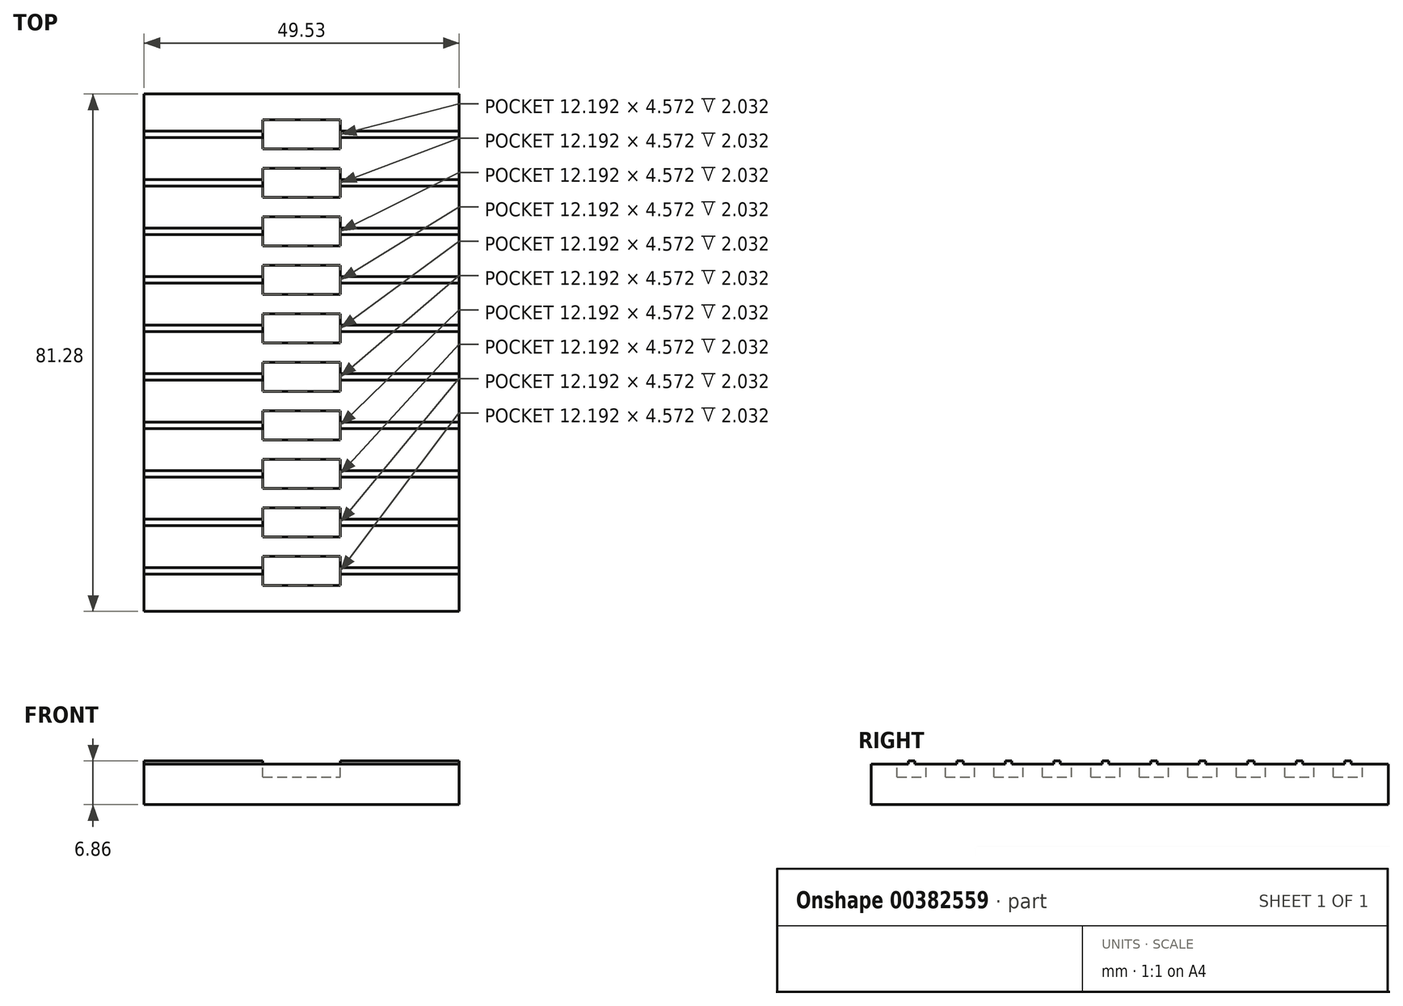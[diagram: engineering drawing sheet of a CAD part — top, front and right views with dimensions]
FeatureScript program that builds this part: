
annotation { "Feature Type Name" : "Feature", "Feature Type Description" : "" }
export const myFeature = defineFeature(function(context is Context, id is Id, definition is map)
    precondition{}
    {
        {
            var Q0;
            Q0=qCreatedBy(makeId("Top.planeOp"),FACE);
            var sketch = newSketch(context, id + "F0", { "sketchPlane" : qUnion([Q0])});
            skLineSegment(sketch, "E0.bottom", {"start": v(0, 0) * mm, "end": v(49.53, 0) * mm});
            skLineSegment(sketch, "E0.top", {"start": v(0, 81.28) * mm, "end": v(49.53, 81.28) * mm});
            skLineSegment(sketch, "E0.left", {"start": v(0, 0) * mm, "end": v(0, 81.28) * mm});
            skLineSegment(sketch, "E0.right", {"start": v(49.53, 0) * mm, "end": v(49.53, 81.28) * mm});
            skSolve(sketch);
        }
        {
            var Q0;
            Q0=qSketchRegion(id+"F0",true);
            extrude(context, id + "F1", {"entities" : qUnion([Q0]), "depth" : 6.35 * mm});
        }
        {
            var Q0;
            Q0=makeQuery(id+"F1.opExtrude","CAP_FACE",FACE,{"disambiguationData":[OSD([sQuery(id+"F0.wireOp",EDGE,"E0.bottom"),sQuery(id+"F0.wireOp",EDGE,"E0.top"),sQuery(id+"F0.wireOp",EDGE,"E0.left"),sQuery(id+"F0.wireOp",EDGE,"E0.right")])],"isStart":false});
            var sketch = newSketch(context, id + "F2", { "sketchPlane" : qUnion([Q0])});
            skLineSegment(sketch, "E1.bottom", {"start": v(18.67, 4.06) * mm, "end": v(30.86, 4.06) * mm});
            skLineSegment(sketch, "E1.top", {"start": v(18.67, 8.64) * mm, "end": v(30.86, 8.64) * mm});
            skLineSegment(sketch, "E1.left", {"start": v(18.67, 4.06) * mm, "end": v(18.67, 8.64) * mm});
            skLineSegment(sketch, "E1.right", {"start": v(30.86, 4.06) * mm, "end": v(30.86, 8.64) * mm});
            skLineSegment(sketch, "E2", {"start": v(30.86, 6.35) * mm, "end": v(49.53, 6.35) * mm, "construction": true});
            skLineSegment(sketch, "E3.0.1.0", {"start": v(18.67, 16.26) * mm, "end": v(30.86, 16.26) * mm});
            skLineSegment(sketch, "E3.0.1.1", {"start": v(18.67, 11.68) * mm, "end": v(30.86, 11.68) * mm});
            skLineSegment(sketch, "E3.0.1.2", {"start": v(30.86, 11.68) * mm, "end": v(30.86, 16.26) * mm});
            skLineSegment(sketch, "E3.0.1.3", {"start": v(18.67, 11.68) * mm, "end": v(18.67, 16.26) * mm});
            skLineSegment(sketch, "E3.0.2.0", {"start": v(18.67, 23.88) * mm, "end": v(30.86, 23.88) * mm});
            skLineSegment(sketch, "E3.0.2.1", {"start": v(18.67, 19.3) * mm, "end": v(30.86, 19.3) * mm});
            skLineSegment(sketch, "E3.0.2.2", {"start": v(30.86, 19.3) * mm, "end": v(30.86, 23.88) * mm});
            skLineSegment(sketch, "E3.0.2.3", {"start": v(18.67, 19.3) * mm, "end": v(18.67, 23.88) * mm});
            skLineSegment(sketch, "E3.0.3.0", {"start": v(18.67, 31.5) * mm, "end": v(30.86, 31.5) * mm});
            skLineSegment(sketch, "E3.0.3.1", {"start": v(18.67, 26.92) * mm, "end": v(30.86, 26.92) * mm});
            skLineSegment(sketch, "E3.0.3.2", {"start": v(30.86, 26.92) * mm, "end": v(30.86, 31.5) * mm});
            skLineSegment(sketch, "E3.0.3.3", {"start": v(18.67, 26.92) * mm, "end": v(18.67, 31.5) * mm});
            skLineSegment(sketch, "E3.0.4.0", {"start": v(18.67, 39.12) * mm, "end": v(30.86, 39.12) * mm});
            skLineSegment(sketch, "E3.0.4.1", {"start": v(18.67, 34.54) * mm, "end": v(30.86, 34.54) * mm});
            skLineSegment(sketch, "E3.0.4.2", {"start": v(30.86, 34.54) * mm, "end": v(30.86, 39.12) * mm});
            skLineSegment(sketch, "E3.0.4.3", {"start": v(18.67, 34.54) * mm, "end": v(18.67, 39.12) * mm});
            skLineSegment(sketch, "E3.0.5.0", {"start": v(18.67, 46.74) * mm, "end": v(30.86, 46.74) * mm});
            skLineSegment(sketch, "E3.0.5.1", {"start": v(18.67, 42.16) * mm, "end": v(30.86, 42.16) * mm});
            skLineSegment(sketch, "E3.0.5.2", {"start": v(30.86, 42.16) * mm, "end": v(30.86, 46.74) * mm});
            skLineSegment(sketch, "E3.0.5.3", {"start": v(18.67, 42.16) * mm, "end": v(18.67, 46.74) * mm});
            skLineSegment(sketch, "E3.0.6.0", {"start": v(18.67, 54.36) * mm, "end": v(30.86, 54.36) * mm});
            skLineSegment(sketch, "E3.0.6.1", {"start": v(18.67, 49.78) * mm, "end": v(30.86, 49.78) * mm});
            skLineSegment(sketch, "E3.0.6.2", {"start": v(30.86, 49.78) * mm, "end": v(30.86, 54.36) * mm});
            skLineSegment(sketch, "E3.0.6.3", {"start": v(18.67, 49.78) * mm, "end": v(18.67, 54.36) * mm});
            skLineSegment(sketch, "E3.0.7.0", {"start": v(18.67, 61.98) * mm, "end": v(30.86, 61.98) * mm});
            skLineSegment(sketch, "E3.0.7.1", {"start": v(18.67, 57.4) * mm, "end": v(30.86, 57.4) * mm});
            skLineSegment(sketch, "E3.0.7.2", {"start": v(30.86, 57.4) * mm, "end": v(30.86, 61.98) * mm});
            skLineSegment(sketch, "E3.0.7.3", {"start": v(18.67, 57.4) * mm, "end": v(18.67, 61.98) * mm});
            skLineSegment(sketch, "E3.0.8.0", {"start": v(18.67, 69.6) * mm, "end": v(30.86, 69.6) * mm});
            skLineSegment(sketch, "E3.0.8.1", {"start": v(18.67, 65.02) * mm, "end": v(30.86, 65.02) * mm});
            skLineSegment(sketch, "E3.0.8.2", {"start": v(30.86, 65.02) * mm, "end": v(30.86, 69.6) * mm});
            skLineSegment(sketch, "E3.0.8.3", {"start": v(18.67, 65.02) * mm, "end": v(18.67, 69.6) * mm});
            skLineSegment(sketch, "E3.0.9.0", {"start": v(18.67, 77.22) * mm, "end": v(30.86, 77.22) * mm});
            skLineSegment(sketch, "E3.0.9.1", {"start": v(18.67, 72.64) * mm, "end": v(30.86, 72.64) * mm});
            skLineSegment(sketch, "E3.0.9.2", {"start": v(30.86, 72.64) * mm, "end": v(30.86, 77.22) * mm});
            skLineSegment(sketch, "E3.0.9.3", {"start": v(18.67, 72.64) * mm, "end": v(18.67, 77.22) * mm});
            skLineSegment(sketch, "E3.direction1", {"start": v(18.67, 4.06) * mm, "end": v(44.2, 4.06) * mm, "construction": true});
            skLineSegment(sketch, "E3.direction2", {"start": v(18.67, 4.06) * mm, "end": v(18.67, 11.68) * mm, "construction": true});
            skSolve(sketch);
        }
        {
            var Q0;
            Q0=qSketchRegion(id+"F2",true);
            extrude(context, id + "F3", {"entities" : qUnion([Q0]), "operationType" : NewBodyOperationType.REMOVE, "oppositeDirection" : true, "depth" : 2.03 * mm});
        }
        {
            var Q0;
            Q0=makeQuery(id+"F1.opExtrude","CAP_FACE",FACE,{"disambiguationData":[OSD([sQuery(id+"F0.wireOp",EDGE,"E0.bottom"),sQuery(id+"F0.wireOp",EDGE,"E0.top"),sQuery(id+"F0.wireOp",EDGE,"E0.left"),sQuery(id+"F0.wireOp",EDGE,"E0.right")])],"isStart":false});
            var sketch = newSketch(context, id + "F4", { "sketchPlane" : qUnion([Q0])});
            skLineSegment(sketch, "E4.bottom", {"start": v(30.86, 5.84) * mm, "end": v(49.53, 5.84) * mm});
            skLineSegment(sketch, "E4.top", {"start": v(30.86, 6.86) * mm, "end": v(49.53, 6.86) * mm});
            skLineSegment(sketch, "E4.left", {"start": v(30.86, 5.84) * mm, "end": v(30.86, 6.86) * mm});
            skLineSegment(sketch, "E4.right", {"start": v(49.53, 5.84) * mm, "end": v(49.53, 6.86) * mm});
            skPoint(sketch, "E5.firstSnap0", {"position": v(40.2, 6.86) * mm});
            skLineSegment(sketch, "E5.bottom", {"start": v(18.67, 6.86) * mm, "end": v(0, 6.86) * mm});
            skLineSegment(sketch, "E5.top", {"start": v(18.67, 5.84) * mm, "end": v(0, 5.84) * mm});
            skLineSegment(sketch, "E5.left", {"start": v(18.67, 6.86) * mm, "end": v(18.67, 5.84) * mm});
            skLineSegment(sketch, "E5.right", {"start": v(0, 6.86) * mm, "end": v(0, 5.84) * mm});
            skLineSegment(sketch, "E6", {"start": v(30.86, 6.35) * mm, "end": v(49.53, 6.35) * mm, "construction": true});
            skLineSegment(sketch, "E7.0.1.0", {"start": v(18.67, 13.46) * mm, "end": v(0, 13.46) * mm});
            skLineSegment(sketch, "E7.0.1.1", {"start": v(30.86, 13.97) * mm, "end": v(49.53, 13.97) * mm, "construction": true});
            skLineSegment(sketch, "E7.0.1.2", {"start": v(18.67, 14.48) * mm, "end": v(0, 14.48) * mm});
            skLineSegment(sketch, "E7.0.1.3", {"start": v(30.86, 14.48) * mm, "end": v(49.53, 14.48) * mm});
            skLineSegment(sketch, "E7.0.1.4", {"start": v(30.86, 13.46) * mm, "end": v(49.53, 13.46) * mm});
            skPoint(sketch, "E7.0.1.5", {"position": v(40.2, 14.48) * mm});
            skLineSegment(sketch, "E7.0.1.6", {"start": v(18.67, 14.48) * mm, "end": v(18.67, 13.46) * mm});
            skLineSegment(sketch, "E7.0.1.7", {"start": v(0, 14.48) * mm, "end": v(0, 13.46) * mm});
            skLineSegment(sketch, "E7.0.1.8", {"start": v(49.53, 13.46) * mm, "end": v(49.53, 14.48) * mm});
            skLineSegment(sketch, "E7.0.1.9", {"start": v(30.86, 13.46) * mm, "end": v(30.86, 14.48) * mm});
            skLineSegment(sketch, "E7.0.2.0", {"start": v(18.67, 21.08) * mm, "end": v(0, 21.08) * mm});
            skLineSegment(sketch, "E7.0.2.1", {"start": v(30.86, 21.6) * mm, "end": v(49.53, 21.6) * mm, "construction": true});
            skLineSegment(sketch, "E7.0.2.2", {"start": v(18.67, 22.1) * mm, "end": v(0, 22.1) * mm});
            skLineSegment(sketch, "E7.0.2.3", {"start": v(30.86, 22.1) * mm, "end": v(49.53, 22.1) * mm});
            skLineSegment(sketch, "E7.0.2.4", {"start": v(30.86, 21.08) * mm, "end": v(49.53, 21.08) * mm});
            skPoint(sketch, "E7.0.2.5", {"position": v(40.2, 22.1) * mm});
            skLineSegment(sketch, "E7.0.2.6", {"start": v(18.67, 22.1) * mm, "end": v(18.67, 21.08) * mm});
            skLineSegment(sketch, "E7.0.2.7", {"start": v(0, 22.1) * mm, "end": v(0, 21.08) * mm});
            skLineSegment(sketch, "E7.0.2.8", {"start": v(49.53, 21.08) * mm, "end": v(49.53, 22.1) * mm});
            skLineSegment(sketch, "E7.0.2.9", {"start": v(30.86, 21.08) * mm, "end": v(30.86, 22.1) * mm});
            skLineSegment(sketch, "E7.0.3.0", {"start": v(18.67, 28.7) * mm, "end": v(0, 28.7) * mm});
            skLineSegment(sketch, "E7.0.3.1", {"start": v(30.86, 29.21) * mm, "end": v(49.53, 29.21) * mm, "construction": true});
            skLineSegment(sketch, "E7.0.3.2", {"start": v(18.67, 29.72) * mm, "end": v(0, 29.72) * mm});
            skLineSegment(sketch, "E7.0.3.3", {"start": v(30.86, 29.72) * mm, "end": v(49.53, 29.72) * mm});
            skLineSegment(sketch, "E7.0.3.4", {"start": v(30.86, 28.7) * mm, "end": v(49.53, 28.7) * mm});
            skPoint(sketch, "E7.0.3.5", {"position": v(40.2, 29.72) * mm});
            skLineSegment(sketch, "E7.0.3.6", {"start": v(18.67, 29.72) * mm, "end": v(18.67, 28.7) * mm});
            skLineSegment(sketch, "E7.0.3.7", {"start": v(0, 29.72) * mm, "end": v(0, 28.7) * mm});
            skLineSegment(sketch, "E7.0.3.8", {"start": v(49.53, 28.7) * mm, "end": v(49.53, 29.72) * mm});
            skLineSegment(sketch, "E7.0.3.9", {"start": v(30.86, 28.7) * mm, "end": v(30.86, 29.72) * mm});
            skLineSegment(sketch, "E7.0.4.0", {"start": v(18.67, 36.32) * mm, "end": v(0, 36.32) * mm});
            skLineSegment(sketch, "E7.0.4.1", {"start": v(30.86, 36.83) * mm, "end": v(49.53, 36.83) * mm, "construction": true});
            skLineSegment(sketch, "E7.0.4.2", {"start": v(18.67, 37.34) * mm, "end": v(0, 37.34) * mm});
            skLineSegment(sketch, "E7.0.4.3", {"start": v(30.86, 37.34) * mm, "end": v(49.53, 37.34) * mm});
            skLineSegment(sketch, "E7.0.4.4", {"start": v(30.86, 36.32) * mm, "end": v(49.53, 36.32) * mm});
            skPoint(sketch, "E7.0.4.5", {"position": v(40.2, 37.34) * mm});
            skLineSegment(sketch, "E7.0.4.6", {"start": v(18.67, 37.34) * mm, "end": v(18.67, 36.32) * mm});
            skLineSegment(sketch, "E7.0.4.7", {"start": v(0, 37.34) * mm, "end": v(0, 36.32) * mm});
            skLineSegment(sketch, "E7.0.4.8", {"start": v(49.53, 36.32) * mm, "end": v(49.53, 37.34) * mm});
            skLineSegment(sketch, "E7.0.4.9", {"start": v(30.86, 36.32) * mm, "end": v(30.86, 37.34) * mm});
            skLineSegment(sketch, "E7.0.5.0", {"start": v(18.67, 43.94) * mm, "end": v(0, 43.94) * mm});
            skLineSegment(sketch, "E7.0.5.1", {"start": v(30.86, 44.45) * mm, "end": v(49.53, 44.45) * mm, "construction": true});
            skLineSegment(sketch, "E7.0.5.2", {"start": v(18.67, 44.96) * mm, "end": v(0, 44.96) * mm});
            skLineSegment(sketch, "E7.0.5.3", {"start": v(30.86, 44.96) * mm, "end": v(49.53, 44.96) * mm});
            skLineSegment(sketch, "E7.0.5.4", {"start": v(30.86, 43.94) * mm, "end": v(49.53, 43.94) * mm});
            skPoint(sketch, "E7.0.5.5", {"position": v(40.2, 44.96) * mm});
            skLineSegment(sketch, "E7.0.5.6", {"start": v(18.67, 44.96) * mm, "end": v(18.67, 43.94) * mm});
            skLineSegment(sketch, "E7.0.5.7", {"start": v(0, 44.96) * mm, "end": v(0, 43.94) * mm});
            skLineSegment(sketch, "E7.0.5.8", {"start": v(49.53, 43.94) * mm, "end": v(49.53, 44.96) * mm});
            skLineSegment(sketch, "E7.0.5.9", {"start": v(30.86, 43.94) * mm, "end": v(30.86, 44.96) * mm});
            skLineSegment(sketch, "E7.0.6.0", {"start": v(18.67, 51.56) * mm, "end": v(0, 51.56) * mm});
            skLineSegment(sketch, "E7.0.6.1", {"start": v(30.86, 52.07) * mm, "end": v(49.53, 52.07) * mm, "construction": true});
            skLineSegment(sketch, "E7.0.6.2", {"start": v(18.67, 52.58) * mm, "end": v(0, 52.58) * mm});
            skLineSegment(sketch, "E7.0.6.3", {"start": v(30.86, 52.58) * mm, "end": v(49.53, 52.58) * mm});
            skLineSegment(sketch, "E7.0.6.4", {"start": v(30.86, 51.56) * mm, "end": v(49.53, 51.56) * mm});
            skPoint(sketch, "E7.0.6.5", {"position": v(40.2, 52.58) * mm});
            skLineSegment(sketch, "E7.0.6.6", {"start": v(18.67, 52.58) * mm, "end": v(18.67, 51.56) * mm});
            skLineSegment(sketch, "E7.0.6.7", {"start": v(0, 52.58) * mm, "end": v(0, 51.56) * mm});
            skLineSegment(sketch, "E7.0.6.8", {"start": v(49.53, 51.56) * mm, "end": v(49.53, 52.58) * mm});
            skLineSegment(sketch, "E7.0.6.9", {"start": v(30.86, 51.56) * mm, "end": v(30.86, 52.58) * mm});
            skLineSegment(sketch, "E7.0.7.0", {"start": v(18.67, 59.18) * mm, "end": v(0, 59.18) * mm});
            skLineSegment(sketch, "E7.0.7.1", {"start": v(30.86, 59.69) * mm, "end": v(49.53, 59.69) * mm, "construction": true});
            skLineSegment(sketch, "E7.0.7.2", {"start": v(18.67, 60.2) * mm, "end": v(0, 60.2) * mm});
            skLineSegment(sketch, "E7.0.7.3", {"start": v(30.86, 60.2) * mm, "end": v(49.53, 60.2) * mm});
            skLineSegment(sketch, "E7.0.7.4", {"start": v(30.86, 59.18) * mm, "end": v(49.53, 59.18) * mm});
            skPoint(sketch, "E7.0.7.5", {"position": v(40.2, 60.2) * mm});
            skLineSegment(sketch, "E7.0.7.6", {"start": v(18.67, 60.2) * mm, "end": v(18.67, 59.18) * mm});
            skLineSegment(sketch, "E7.0.7.7", {"start": v(0, 60.2) * mm, "end": v(0, 59.18) * mm});
            skLineSegment(sketch, "E7.0.7.8", {"start": v(49.53, 59.18) * mm, "end": v(49.53, 60.2) * mm});
            skLineSegment(sketch, "E7.0.7.9", {"start": v(30.86, 59.18) * mm, "end": v(30.86, 60.2) * mm});
            skLineSegment(sketch, "E7.0.8.0", {"start": v(18.67, 66.8) * mm, "end": v(0, 66.8) * mm});
            skLineSegment(sketch, "E7.0.8.1", {"start": v(30.86, 67.3) * mm, "end": v(49.53, 67.3) * mm, "construction": true});
            skLineSegment(sketch, "E7.0.8.2", {"start": v(18.67, 67.82) * mm, "end": v(0, 67.82) * mm});
            skLineSegment(sketch, "E7.0.8.3", {"start": v(30.86, 67.82) * mm, "end": v(49.53, 67.82) * mm});
            skLineSegment(sketch, "E7.0.8.4", {"start": v(30.86, 66.8) * mm, "end": v(49.53, 66.8) * mm});
            skPoint(sketch, "E7.0.8.5", {"position": v(40.2, 67.82) * mm});
            skLineSegment(sketch, "E7.0.8.6", {"start": v(18.67, 67.82) * mm, "end": v(18.67, 66.8) * mm});
            skLineSegment(sketch, "E7.0.8.7", {"start": v(0, 67.82) * mm, "end": v(0, 66.8) * mm});
            skLineSegment(sketch, "E7.0.8.8", {"start": v(49.53, 66.8) * mm, "end": v(49.53, 67.82) * mm});
            skLineSegment(sketch, "E7.0.8.9", {"start": v(30.86, 66.8) * mm, "end": v(30.86, 67.82) * mm});
            skLineSegment(sketch, "E7.0.9.0", {"start": v(18.67, 74.42) * mm, "end": v(0, 74.42) * mm});
            skLineSegment(sketch, "E7.0.9.1", {"start": v(30.86, 74.93) * mm, "end": v(49.53, 74.93) * mm, "construction": true});
            skLineSegment(sketch, "E7.0.9.2", {"start": v(18.67, 75.44) * mm, "end": v(0, 75.44) * mm});
            skLineSegment(sketch, "E7.0.9.3", {"start": v(30.86, 75.44) * mm, "end": v(49.53, 75.44) * mm});
            skLineSegment(sketch, "E7.0.9.4", {"start": v(30.86, 74.42) * mm, "end": v(49.53, 74.42) * mm});
            skPoint(sketch, "E7.0.9.5", {"position": v(40.2, 75.44) * mm});
            skLineSegment(sketch, "E7.0.9.6", {"start": v(18.67, 75.44) * mm, "end": v(18.67, 74.42) * mm});
            skLineSegment(sketch, "E7.0.9.7", {"start": v(0, 75.44) * mm, "end": v(0, 74.42) * mm});
            skLineSegment(sketch, "E7.0.9.8", {"start": v(49.53, 74.42) * mm, "end": v(49.53, 75.44) * mm});
            skLineSegment(sketch, "E7.0.9.9", {"start": v(30.86, 74.42) * mm, "end": v(30.86, 75.44) * mm});
            skLineSegment(sketch, "E7.direction1", {"start": v(0, 5.84) * mm, "end": v(25.4, 5.84) * mm, "construction": true});
            skLineSegment(sketch, "E7.direction2", {"start": v(0, 5.84) * mm, "end": v(0, 13.46) * mm, "construction": true});
            skSolve(sketch);
        }
        {
            var Q0;
            Q0=qSketchRegion(id+"F4",true);
            extrude(context, id + "F5", {"entities" : qUnion([Q0]), "operationType" : NewBodyOperationType.ADD, "depth" : 0.5 * mm});
        }
    });
